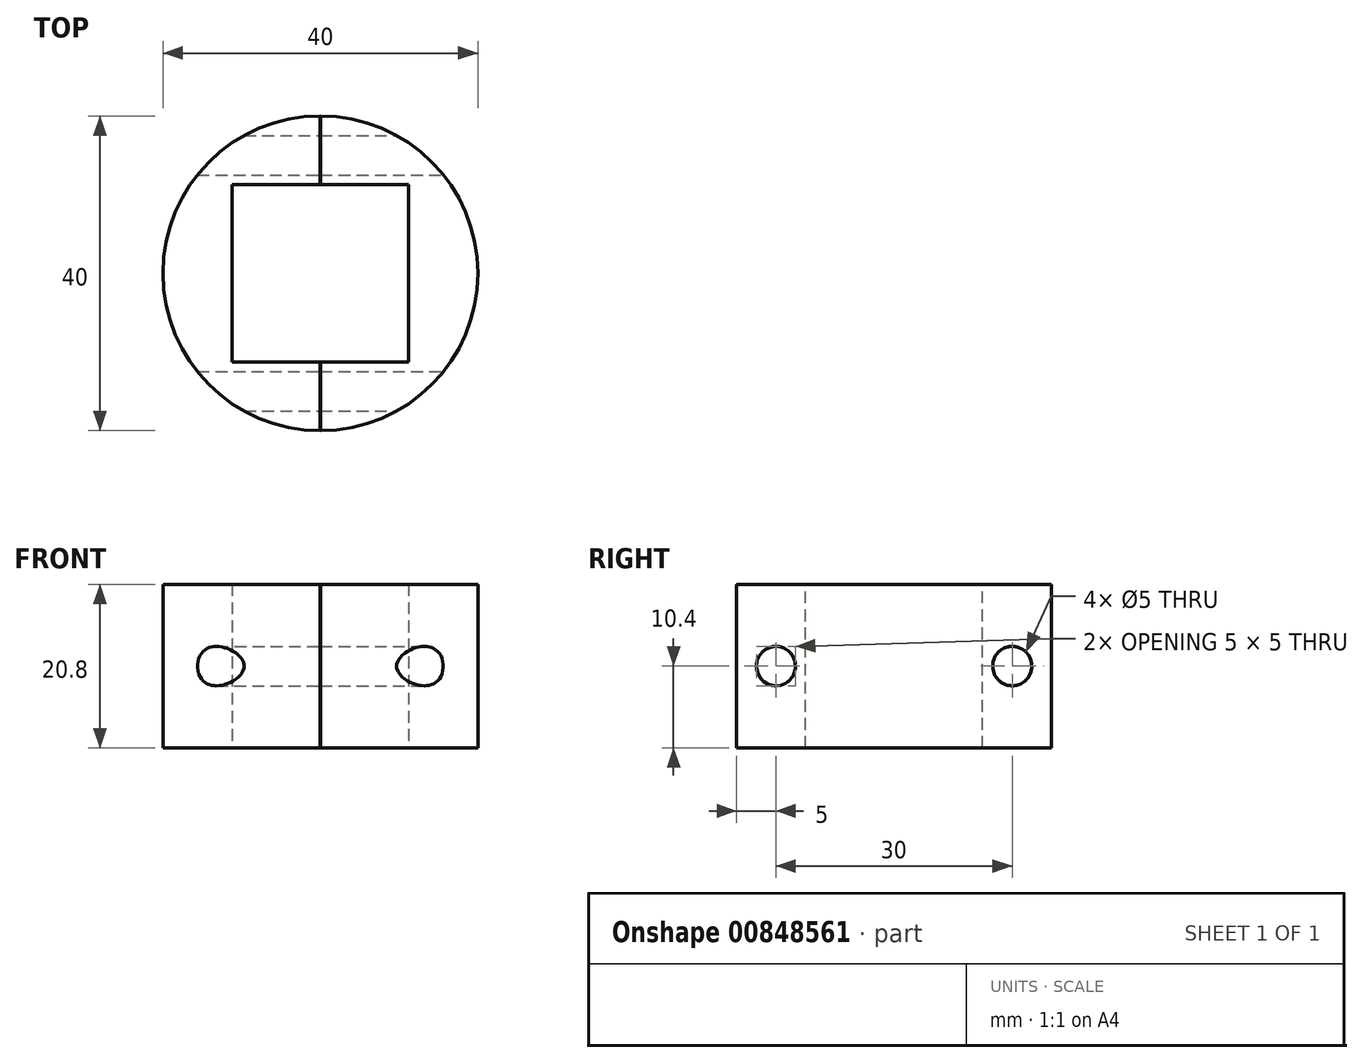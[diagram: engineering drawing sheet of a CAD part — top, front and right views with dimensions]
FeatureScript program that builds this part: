
annotation { "Feature Type Name" : "Feature", "Feature Type Description" : "" }
export const myFeature = defineFeature(function(context is Context, id is Id, definition is map)
    precondition{}
    {
        {
            var Q0;
            Q0=qCreatedBy(makeId("Top.planeOp"),FACE);
            var sketch = newSketch(context, id + "F0", { "sketchPlane" : qUnion([Q0])});
            skCircle(sketch, "E0", {"center": v(0, 0) * mm, "radius": 20 * mm});
            skLineSegment(sketch, "E1.bottom", {"start": v(-11.2, 11.25) * mm, "end": v(11.2, 11.25) * mm});
            skLineSegment(sketch, "E1.top", {"start": v(-11.2, -11.25) * mm, "end": v(11.2, -11.25) * mm});
            skLineSegment(sketch, "E1.left", {"start": v(-11.2, 11.25) * mm, "end": v(-11.2, -11.25) * mm});
            skLineSegment(sketch, "E1.right", {"start": v(11.2, 11.25) * mm, "end": v(11.2, -11.25) * mm});
            skLineSegment(sketch, "E2", {"start": v(0, 11.25) * mm, "end": v(0, -11.25) * mm, "construction": true});
            skLineSegment(sketch, "E3", {"start": v(11.2, 0) * mm, "end": v(-11.2, 0) * mm, "construction": true});
            skSolve(sketch);
        }
        {
            var Q0;
            Q0=makeQuery(id+"F0.imprint","IMPRINT",FACE,{"disambiguationData":[TD([[makeQuery(id+"F0.imprint","IMPRINT",EDGE,{"derivedFrom":sQuery(id+"F0.wireOp",EDGE,"E0")}),1.0]])]});
            extrude(context, id + "F1", {"entities" : qUnion([Q0]), "depth" : 20.8 * mm, "offsetDistance" : 25 * mm});
        }
        {
            var Q0;
            Q0=qCreatedBy(makeId("Right.planeOp"),FACE);
            cPlane(context, id + "F2", {"entities" : qUnion([Q0]), "cplaneType" : CPlaneType.OFFSET, "offset" : 20 * mm, "width" : 150 * mm, "height" : 150 * mm});
        }
        {
            var Q0;
            Q0=qCreatedBy(id+"F2.planeOp",FACE);
            var sketch = newSketch(context, id + "F3", { "sketchPlane" : qUnion([Q0])});
            skCircle(sketch, "E4", {"center": v(-15, 10.4) * mm, "radius": 2.5 * mm});
            skCircle(sketch, "E5", {"center": v(15, 10.4) * mm, "radius": 2.5 * mm});
            skSolve(sketch);
        }
        {
            var Q0;
            Q0=makeQuery(id+"F3.imprint","IMPRINT",FACE,{"disambiguationData":[TD([[makeQuery(id+"F3.imprint","IMPRINT",EDGE,{"derivedFrom":sQuery(id+"F3.wireOp",EDGE,"E4")}),1.0]])]});
            var Q1;
            Q1=makeQuery(id+"F3.imprint","IMPRINT",FACE,{"disambiguationData":[TD([[makeQuery(id+"F3.imprint","IMPRINT",EDGE,{"derivedFrom":sQuery(id+"F3.wireOp",EDGE,"E5")}),1.0]])]});
            extrude(context, id + "F4", {"entities" : qUnion([Q0, Q1]), "operationType" : NewBodyOperationType.REMOVE, "endBound" : BoundingType.THROUGH_ALL, "oppositeDirection" : true, "depth" : 25 * mm, "offsetDistance" : 25 * mm});
        }
        {
            var Q0;
            Q0=makeQuery(id+"F1.opExtrude","CAP_FACE",FACE,{"disambiguationData":[OSD([sQuery(id+"F0.wireOp",EDGE,"E0"),sQuery(id+"F0.wireOp",EDGE,"E1.bottom"),sQuery(id+"F0.wireOp",EDGE,"E1.top"),sQuery(id+"F0.wireOp",EDGE,"E1.left"),sQuery(id+"F0.wireOp",EDGE,"E1.right")])],"isStart":false});
            var sketch = newSketch(context, id + "F5", { "sketchPlane" : qUnion([Q0])});
            skLineSegment(sketch, "E6.bottom", {"start": v(0.02, 25) * mm, "end": v(-0.02, 25) * mm});
            skLineSegment(sketch, "E6.top", {"start": v(0.02, -25) * mm, "end": v(-0.02, -25) * mm});
            skLineSegment(sketch, "E6.left", {"start": v(0.02, 25) * mm, "end": v(0.01, -25) * mm});
            skLineSegment(sketch, "E6.right", {"start": v(-0.01, 25) * mm, "end": v(-0.02, -25) * mm});
            skPoint(sketch, "E7", {"position": v(0, -25) * mm});
            skPoint(sketch, "E8", {"position": v(0.02, 0) * mm});
            skSolve(sketch);
        }
        {
            var Q0;
            Q0 = qSketchRegion(id + "F5", true);
            extrude(context, id + "F6", {"entities" : qUnion([Q0]), "operationType" : NewBodyOperationType.REMOVE, "endBound" : BoundingType.THROUGH_ALL, "oppositeDirection" : true, "depth" : 25 * mm, "offsetDistance" : 25 * mm});
        }
    });
